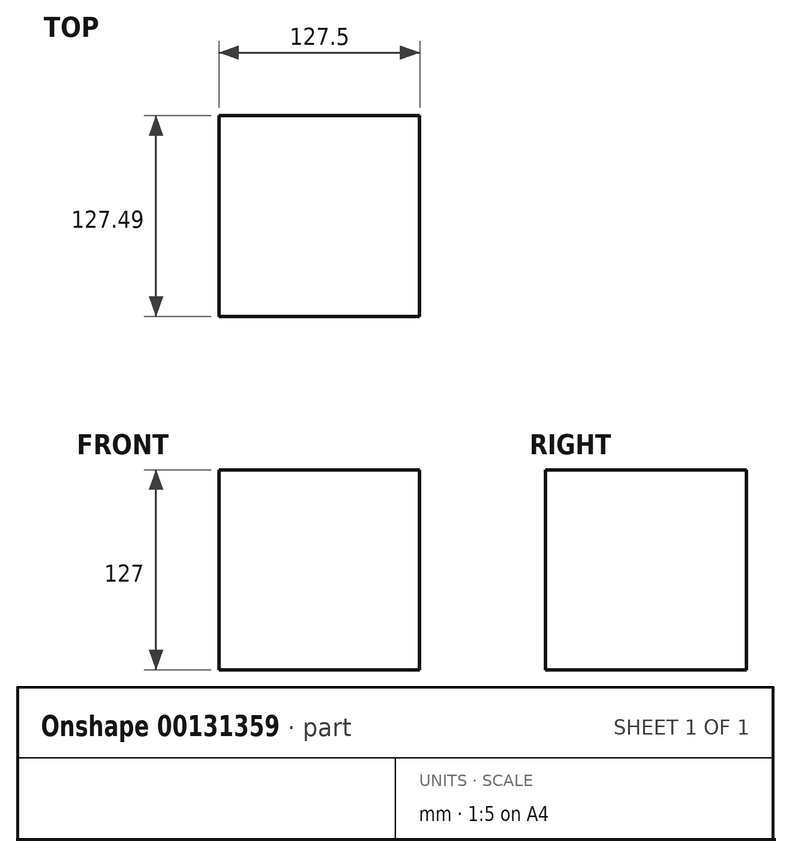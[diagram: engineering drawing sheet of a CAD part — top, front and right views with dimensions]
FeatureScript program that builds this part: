
annotation { "Feature Type Name" : "Feature", "Feature Type Description" : "" }
export const myFeature = defineFeature(function(context is Context, id is Id, definition is map)
    precondition{}
    {
        {
            var Q0;
            Q0=qCreatedBy(makeId("Top.planeOp"),FACE);
            var sketch = newSketch(context, id + "F0", { "sketchPlane" : qUnion([Q0])});
            skLineSegment(sketch, "E0.bottom", {"start": v(-74.64, -73.04) * mm, "end": v(52.86, -73.04) * mm});
            skLineSegment(sketch, "E0.top", {"start": v(-74.64, 54.45) * mm, "end": v(52.86, 54.45) * mm});
            skLineSegment(sketch, "E0.left", {"start": v(-74.64, -73.04) * mm, "end": v(-74.64, 54.45) * mm});
            skLineSegment(sketch, "E0.right", {"start": v(52.86, -73.04) * mm, "end": v(52.86, 54.45) * mm});
            skSolve(sketch);
        }
        {
            var Q0;
            Q0=makeQuery(id+"F0.imprint","IMPRINT",FACE,{"disambiguationData":[TD([[makeQuery(id+"F0.imprint","IMPRINT",EDGE,{"derivedFrom":sQuery(id+"F0.wireOp",EDGE,"E0.bottom")}),1.0]])]});
            var Q1;
            Q1 = qSketchRegion(id + "F0", true);
            extrude(context, id + "F1", {"entities" : qUnion([Q0, Q1]), "endBound" : BoundingType.SYMMETRIC, "depth" : 127 * mm});
        }
    });
